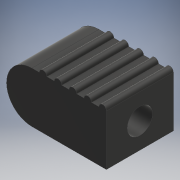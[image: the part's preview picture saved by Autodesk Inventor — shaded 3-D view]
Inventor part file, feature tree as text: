
AUTODESK INVENTOR PART (.ipt)
format: ipt  version: 2017.3 (Build 213256000, 256)  size: 128,512 bytes
history: native  units: mm
features: extrude x3, sketch x3, pattern_linear x1
ambient origin geometry x8: Origin, YZ Plane, XZ Plane, XY Plane, X Axis, Y Axis, Z Axis, Center Point
bodies: Solid1 (feature_tree)
feature tree (7):
  extrude  "Extrusion1"  Depth=6.8mm
  extrude  "Extrusion2"  Depth=9.0mm
  pattern_linear  "Rectangular Pattern1"  Count1=5 Spacing1=2.0mm
  extrude  "Extrusion3"  Depth=3.4mm
  sketch  "Sketch1"  dims[d0=10.0mm d1=6.8mm]
  sketch  "Sketch2"  dims[d2=9.0mm d3=0.0mm d4=1.0mm]
  sketch  "Sketch3"  dims[d5=9.0mm d6=0.0mm d7=50.0mm d9=2.0mm d10=3.4mm d11=4.0mm d12=0.0mm]
